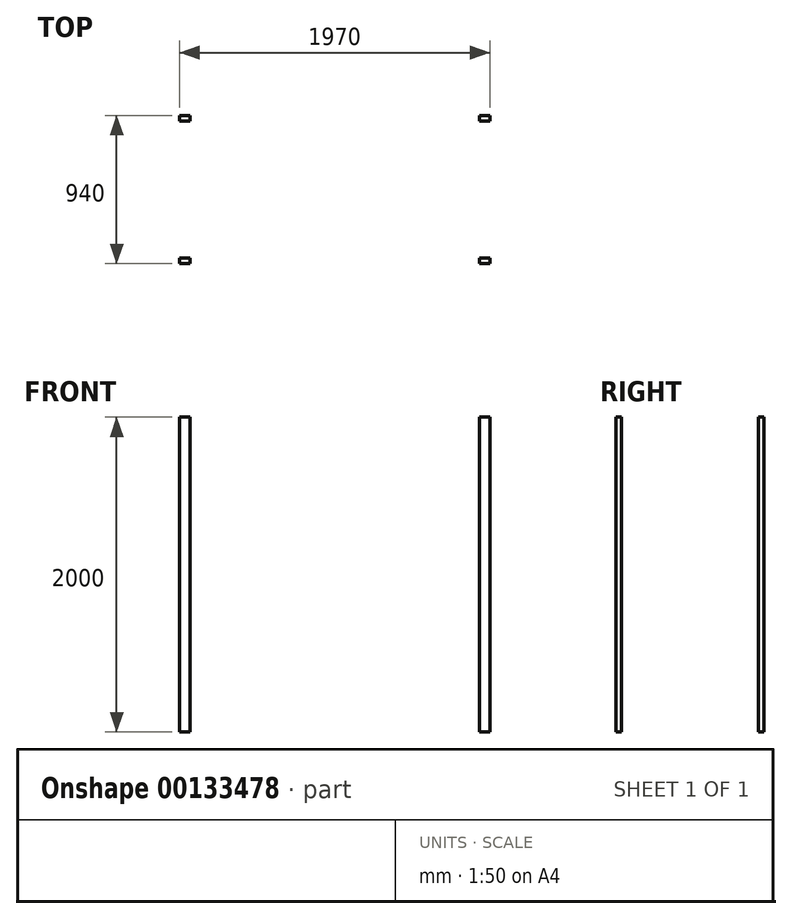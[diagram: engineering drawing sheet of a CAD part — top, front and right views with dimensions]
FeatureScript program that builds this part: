
annotation { "Feature Type Name" : "Feature", "Feature Type Description" : "" }
export const myFeature = defineFeature(function(context is Context, id is Id, definition is map)
    precondition{}
    {
        {
            var Q0;
            Q0=qCreatedBy(makeId("Top.planeOp"),FACE);
            var sketch = newSketch(context, id + "F0", { "sketchPlane" : qUnion([Q0])});
            skLineSegment(sketch, "E0.bottom", {"start": v(-94.95, 140.26) * mm, "end": v(-29.95, 140.26) * mm});
            skLineSegment(sketch, "E0.top", {"start": v(-94.95, 105.26) * mm, "end": v(-29.95, 105.26) * mm});
            skLineSegment(sketch, "E0.left", {"start": v(-94.95, 140.26) * mm, "end": v(-94.95, 105.26) * mm});
            skLineSegment(sketch, "E0.right", {"start": v(-29.95, 140.26) * mm, "end": v(-29.95, 105.26) * mm});
            skLineSegment(sketch, "E1.0.1.0", {"start": v(-94.95, -764.74) * mm, "end": v(-94.95, -799.74) * mm});
            skLineSegment(sketch, "E1.0.1.1", {"start": v(-94.95, -764.74) * mm, "end": v(-29.95, -764.74) * mm});
            skLineSegment(sketch, "E1.0.1.2", {"start": v(-29.95, -764.74) * mm, "end": v(-29.95, -799.74) * mm});
            skLineSegment(sketch, "E1.0.1.3", {"start": v(-94.95, -799.74) * mm, "end": v(-29.95, -799.74) * mm});
            skLineSegment(sketch, "E1.1.0.0", {"start": v(1810.05, 140.26) * mm, "end": v(1810.05, 105.26) * mm});
            skLineSegment(sketch, "E1.1.0.1", {"start": v(1810.05, 140.26) * mm, "end": v(1875.05, 140.26) * mm});
            skLineSegment(sketch, "E1.1.0.2", {"start": v(1875.05, 140.26) * mm, "end": v(1875.05, 105.26) * mm});
            skLineSegment(sketch, "E1.1.0.3", {"start": v(1810.05, 105.26) * mm, "end": v(1875.05, 105.26) * mm});
            skLineSegment(sketch, "E1.1.1.0", {"start": v(1810.05, -764.74) * mm, "end": v(1810.05, -799.74) * mm});
            skLineSegment(sketch, "E1.1.1.1", {"start": v(1810.05, -764.74) * mm, "end": v(1875.05, -764.74) * mm});
            skLineSegment(sketch, "E1.1.1.2", {"start": v(1875.05, -764.74) * mm, "end": v(1875.05, -799.74) * mm});
            skLineSegment(sketch, "E1.1.1.3", {"start": v(1810.05, -799.74) * mm, "end": v(1875.05, -799.74) * mm});
            skLineSegment(sketch, "E1.direction1", {"start": v(-94.95, 105.26) * mm, "end": v(1810.05, 105.26) * mm, "construction": true});
            skLineSegment(sketch, "E1.direction2", {"start": v(-94.95, 105.26) * mm, "end": v(-94.95, -799.74) * mm, "construction": true});
            skSolve(sketch);
        }
        {
            var Q0;
            Q0=makeQuery(id+"F0.imprint","IMPRINT",FACE,{"disambiguationData":[TD([[makeQuery(id+"F0.imprint","IMPRINT",EDGE,{"derivedFrom":sQuery(id+"F0.wireOp",EDGE,"E0.bottom")}),-1.0]])]});
            var Q1;
            Q1=makeQuery(id+"F0.imprint","IMPRINT",FACE,{"disambiguationData":[TD([[makeQuery(id+"F0.imprint","IMPRINT",EDGE,{"derivedFrom":sQuery(id+"F0.wireOp",EDGE,"E1.1.0.0")}),1.0]])]});
            var Q2;
            Q2=makeQuery(id+"F0.imprint","IMPRINT",FACE,{"disambiguationData":[TD([[makeQuery(id+"F0.imprint","IMPRINT",EDGE,{"derivedFrom":sQuery(id+"F0.wireOp",EDGE,"E1.1.1.0")}),1.0]])]});
            var Q3;
            Q3=makeQuery(id+"F0.imprint","IMPRINT",FACE,{"disambiguationData":[TD([[makeQuery(id+"F0.imprint","IMPRINT",EDGE,{"derivedFrom":sQuery(id+"F0.wireOp",EDGE,"E1.0.1.0")}),1.0]])]});
            extrude(context, id + "F1", {"entities" : qUnion([Q0, Q1, Q2, Q3]), "depth" : 2000 * mm});
        }
    });
